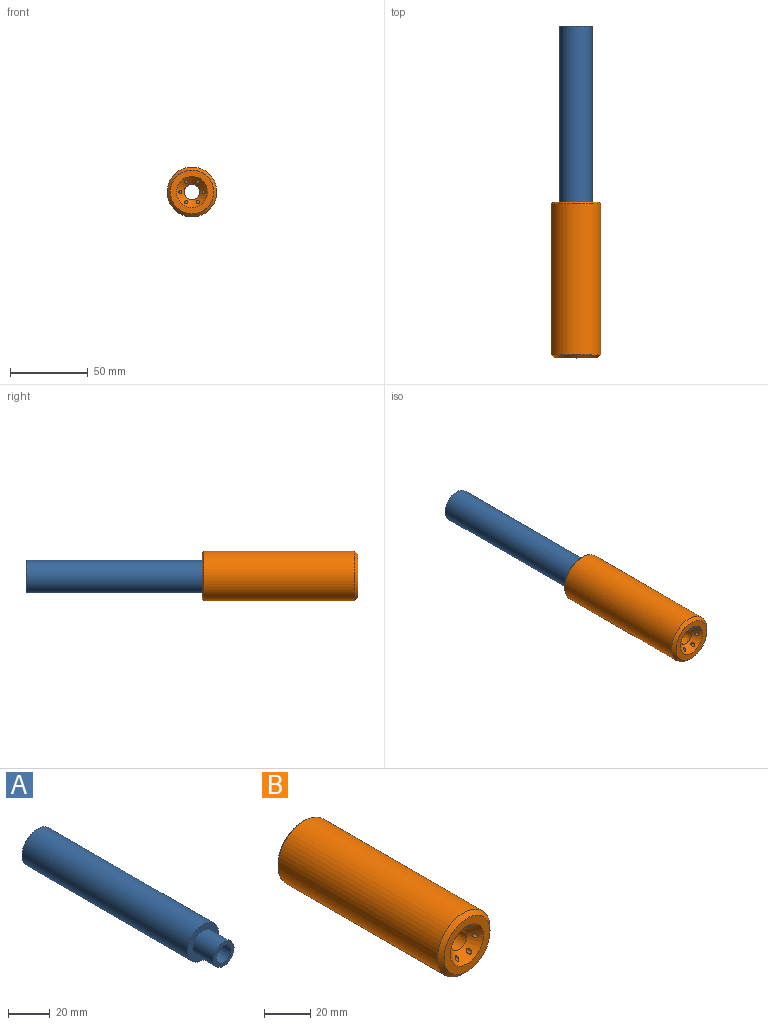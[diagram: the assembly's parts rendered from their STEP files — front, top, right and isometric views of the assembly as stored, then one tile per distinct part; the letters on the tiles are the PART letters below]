
ASSEMBLY  parts=2 mates=1
PART A: 9 faces, bbox 21x127x21 mm
  f0: cylinder r=10.5mm len=113mm, axis (0,1,0), area 7455mm2, adj f1,f2
  f1: plane 21x21mm, normal (0,-1,0), area 192.4mm2, adj f0,f4
  f2: plane 21x21mm, normal (0,1,0), area 91.9mm2, adj f0,f7
  f3: cylinder r=5mm len=111mm, axis (0,1,0), area 3487.2mm2, adj f5,f8
  f4: cylinder r=7mm len=14mm, axis (0,1,0), area 615.8mm2, adj f1,f5
  f5: plane 14x14mm, normal (0,-1,0), area 75.4mm2, adj f3,f4
  f6: cylinder r=7mm len=14mm, axis (0,1,0), area 527.8mm2, adj f7,f8
  f7: cone r=9mm half-angle=45deg, axis (0,1,0), area 142.2mm2, adj f2,f6
  f8: cone r=7mm half-angle=45deg, axis (0,1,0), area 106.6mm2, adj f3,f6
PART B: 173 faces, bbox 32x100x32 mm
  f0: plane 30x30mm, normal (0,1,0), area 493.7mm2, adj f20,f21,f22,f23,f24,f25,f26,f27
  f1: cone r=5mm half-angle=45deg, axis (0,-1,0), area 306.7mm2, adj f3,f4,f8,f10,f12,f14,f16,f18
  f2: cylinder r=16mm len=97mm, axis (0,1,0), area 9751.5mm2, adj f6,f171
  f3: cylinder r=5mm len=79mm, axis (0,1,0), area 2481.9mm2, adj f1,f7
  f4: plane 28x28mm, normal (0,-1,0), area 301.6mm2, adj f1,f6
  f5: cylinder r=7mm len=14mm, axis (0,1,0), area 571.8mm2, adj f7,f172
  f6: cone r=14mm half-angle=45deg, axis (0,1,0), area 266.6mm2, adj f2,f4
  f7: cone r=7mm half-angle=45deg, axis (0,1,0), area 106.6mm2, adj f3,f5
  f8: cylinder r=1mm len=18.5mm, axis (0,1,0), area 110.2mm2, adj f1,f9
  f9: plane 2x2mm, normal (0,-1,0), area 3.1mm2, adj f8
  f10: cylinder r=1mm len=18.5mm, axis (0,1,0), area 110.2mm2, adj f1,f11
  f11: plane 2x2mm, normal (0,-1,0), area 3.1mm2, adj f10
  f12: cylinder r=1mm len=18.5mm, axis (0,1,0), area 110.2mm2, adj f1,f13
  f13: plane 2x2mm, normal (0,-1,0), area 3.1mm2, adj f12
  f14: cylinder r=1mm len=18.5mm, axis (0,1,0), area 110.2mm2, adj f1,f15
  f15: plane 2x2mm, normal (0,-1,0), area 3.1mm2, adj f14
  f16: cylinder r=1mm len=18.5mm, axis (0,1,0), area 110.2mm2, adj f1,f17
  f17: plane 2x2mm, normal (0,-1,0), area 3.1mm2, adj f16
  f18: cylinder r=1mm len=18.5mm, axis (0,1,0), area 110.2mm2, adj f1,f19
  f19: plane 2x2mm, normal (0,-1,0), area 3.1mm2, adj f18
  f20: extruded ~1x0.15mm, area 0.2mm2, adj f0,f21,f36,f37
  f21: extruded ~1x0.23mm, area 0.3mm2, adj f0,f20,f22,f37
  f22: extruded ~1x0.29mm, area 0.3mm2, adj f0,f21,f23,f37
  f23: extruded ~1x0.21mm, area 0.2mm2, adj f0,f22,f24,f37
  f24: extruded ~1x0.2mm, area 0.2mm2, adj f0,f23,f25,f37
  f25: plane 1x0.3mm, normal (-1,0,0), area 0.3mm2, adj f0,f24,f26,f37
  f26: extruded ~1x0.18mm, area 0.2mm2, adj f0,f25,f27,f37
  f27: extruded ~1x0.13mm, area 0.1mm2, adj f0,f26,f28,f37
  f28: extruded ~1x0.16mm, area 0.2mm2, adj f0,f27,f29,f37
  f29: extruded ~1x0.14mm, area 0.2mm2, adj f0,f28,f30,f37
  f30: extruded ~1x0.21mm, area 0.2mm2, adj f0,f29,f31,f37
  f31: plane 1.41x1mm, normal (-1,0,0), area 1.4mm2, adj f0,f30,f32,f37
  f32: plane 1x0.46mm, normal (0,0,1), area 0.5mm2, adj f0,f31,f33,f37
  f33: plane 1.2x1mm, normal (1,0,0), area 1.2mm2, adj f0,f32,f34,f37
  f34: extruded ~1x0.19mm, area 0.2mm2, adj f0,f33,f35,f37
  f35: extruded ~1x0.17mm, area 0.2mm2, adj f0,f34,f36,f37
  f36: extruded ~1x0.16mm, area 0.2mm2, adj f0,f20,f35,f37
  f37: plane 2.16x1.03mm, normal (0,1,0), area 1.1mm2, adj f20,f21,f22,f23,f24,f25,f26,f27
  f38: extruded ~1x0.24mm, area 0.2mm2, adj f0,f39,f53,f54
  f39: extruded ~1x0.2mm, area 0.2mm2, adj f0,f38,f40,f54
  f40: extruded ~1x0.21mm, area 0.2mm2, adj f0,f39,f41,f54
  f41: plane 1x0.3mm, normal (-1,0,0), area 0.3mm2, adj f0,f40,f42,f54
  f42: extruded ~1x0.2mm, area 0.2mm2, adj f0,f41,f43,f54
  f43: extruded ~1x0.11mm, area 0.1mm2, adj f0,f42,f44,f54
  f44: extruded ~1x0.16mm, area 0.2mm2, adj f0,f43,f45,f54
  f45: extruded ~1x0.14mm, area 0.2mm2, adj f0,f44,f46,f54
  f46: extruded ~1x0.21mm, area 0.2mm2, adj f0,f45,f47,f54
  f47: extruded ~1x0.24mm, area 0.2mm2, adj f0,f46,f48,f54
  f48: plane 1.17x1mm, normal (-1,0,0), area 1.2mm2, adj f0,f47,f49,f54
  f49: plane 1x0.46mm, normal (0,0,1), area 0.5mm2, adj f0,f48,f50,f54
  f50: plane 1.46x1mm, normal (1,0,0), area 1.5mm2, adj f0,f49,f51,f54
  f51: extruded ~1x0.28mm, area 0.3mm2, adj f0,f50,f52,f54
  f52: extruded ~1x0.23mm, area 0.3mm2, adj f0,f51,f53,f54
  f53: extruded ~1x0.2mm, area 0.2mm2, adj f0,f38,f52,f54
  f54: plane 2.16x1.03mm, normal (0,1,0), area 1.1mm2, adj f38,f39,f40,f41,f42,f43,f44,f45
  f55: extruded ~1x0.15mm, area 0.2mm2, adj f0,f56,f72,f73
  f56: extruded ~1x0.24mm, area 0.3mm2, adj f0,f55,f57,f73
  f57: extruded ~1x0.29mm, area 0.3mm2, adj f0,f56,f58,f73
  f58: extruded ~1x0.23mm, area 0.2mm2, adj f0,f57,f59,f73
  f59: extruded ~1x0.22mm, area 0.2mm2, adj f0,f58,f60,f73
  f60: plane 1x0.29mm, normal (-1,0,0), area 0.3mm2, adj f0,f59,f61,f73
  f61: extruded ~1x0.17mm, area 0.2mm2, adj f0,f60,f62,f73
  f62: extruded ~1x0.14mm, area 0.1mm2, adj f0,f61,f63,f73
  f63: extruded ~1x0.2mm, area 0.2mm2, adj f0,f62,f64,f73
  f64: extruded ~1x0.14mm, area 0.2mm2, adj f0,f63,f65,f73
  f65: extruded ~1x0.21mm, area 0.2mm2, adj f0,f64,f66,f73
  f66: extruded ~1x0.25mm, area 0.2mm2, adj f0,f65,f67,f73
  f67: plane 1.17x1mm, normal (-1,0,0), area 1.2mm2, adj f0,f66,f68,f73
  f68: plane 1x0.46mm, normal (0,0,1), area 0.5mm2, adj f0,f67,f69,f73
  f69: plane 1.2x1mm, normal (1,0,0), area 1.2mm2, adj f0,f68,f70,f73
  f70: extruded ~1x0.19mm, area 0.2mm2, adj f0,f69,f71,f73
  f71: extruded ~1x0.19mm, area 0.2mm2, adj f0,f70,f72,f73
  f72: extruded ~1x0.18mm, area 0.2mm2, adj f0,f55,f71,f73
  f73: plane 2.16x1.16mm, normal (0,1,0), area 1.1mm2, adj f55,f56,f57,f58,f59,f60,f61,f62
  f74: extruded ~1x0.38mm, area 0.4mm2, adj f0,f75,f89,f90
  f75: plane 1x0.36mm, normal (-1,0,0), area 0.4mm2, adj f0,f74,f76,f90
  f76: extruded ~1x0.18mm, area 0.2mm2, adj f0,f75,f77,f90
  f77: extruded ~1x0.16mm, area 0.2mm2, adj f0,f76,f78,f90
  f78: extruded ~1x0.22mm, area 0.2mm2, adj f0,f77,f79,f90
  f79: extruded ~1x0.26mm, area 0.3mm2, adj f0,f78,f80,f90
  f80: extruded ~1x0.47mm, area 0.5mm2, adj f0,f79,f81,f90
  f81: extruded ~1x0.31mm, area 0.4mm2, adj f0,f80,f82,f90
  f82: plane 1x0.36mm, normal (-1,0,0), area 0.4mm2, adj f0,f81,f83,f90
  f83: extruded ~1x0.37mm, area 0.4mm2, adj f0,f82,f84,f90
  f84: extruded ~1x0.29mm, area 0.4mm2, adj f0,f83,f85,f90
  f85: extruded ~1x0.33mm, area 0.4mm2, adj f0,f84,f86,f90
  f86: extruded ~1x0.41mm, area 0.4mm2, adj f0,f85,f87,f90
  f87: extruded ~1x0.41mm, area 0.4mm2, adj f0,f86,f88,f90
  f88: extruded ~1x0.34mm, area 0.4mm2, adj f0,f87,f89,f90
  f89: extruded ~1x0.29mm, area 0.4mm2, adj f0,f74,f88,f90
  f90: plane 2.17x0.91mm, normal (0,1,0), area 1.1mm2, adj f74,f75,f76,f77,f78,f79,f80,f81
  f91: extruded ~1x0.41mm, area 0.4mm2, adj f0,f92,f106,f107
  f92: extruded ~1x0.41mm, area 0.4mm2, adj f0,f91,f93,f107
  f93: extruded ~1x0.34mm, area 0.4mm2, adj f0,f92,f94,f107
  f94: extruded ~1x0.28mm, area 0.4mm2, adj f0,f93,f95,f107
  f95: extruded ~1x0.38mm, area 0.4mm2, adj f0,f94,f96,f107
  f96: plane 1x0.36mm, normal (1,0,0), area 0.4mm2, adj f0,f95,f97,f107
  f97: extruded ~1x0.18mm, area 0.2mm2, adj f0,f96,f98,f107
  f98: extruded ~1x0.16mm, area 0.2mm2, adj f0,f97,f99,f107
  f99: extruded ~1x0.22mm, area 0.2mm2, adj f0,f98,f100,f107
  f100: extruded ~1x0.27mm, area 0.3mm2, adj f0,f99,f101,f107
  f101: extruded ~1x0.48mm, area 0.5mm2, adj f0,f100,f102,f107
  f102: extruded ~1x0.3mm, area 0.4mm2, adj f0,f101,f103,f107
  f103: plane 1x0.35mm, normal (1,0,0), area 0.4mm2, adj f0,f102,f104,f107
  f104: extruded ~1x0.37mm, area 0.4mm2, adj f0,f103,f105,f107
  f105: extruded ~1x0.29mm, area 0.4mm2, adj f0,f104,f106,f107
  f106: extruded ~1x0.33mm, area 0.4mm2, adj f0,f91,f105,f107
  f107: plane 2.16x0.9mm, normal (0,1,0), area 1.1mm2, adj f91,f92,f93,f94,f95,f96,f97,f98
  f108: plane 1x0.22mm, normal (0.98,0,-0.22), area 0.2mm2, adj f0,f109,f112,f113
  f109: plane 1x0.41mm, normal (0,0,-1), area 0.4mm2, adj f0,f108,f110,f113
  f110: plane 2.14x1mm, normal (-1,0,0), area 2.1mm2, adj f0,f109,f111,f113
  f111: plane 1x0.46mm, normal (0,0,1), area 0.5mm2, adj f0,f110,f112,f113
  f112: plane 1.92x1mm, normal (1,0,0), area 1.9mm2, adj f0,f108,f111,f113
  f113: plane 2.14x0.46mm, normal (0,1,0), area 1mm2, adj f108,f109,f110,f111,f112
  f114: plane 1x0.52mm, normal (0,0,-1), area 0.5mm2, adj f0,f115,f118,f119
  f115: plane 2.07x1mm, normal (-0.96,0,-0.27), area 2.2mm2, adj f0,f114,f116,f119
  f116: plane 1x0.74mm, normal (-1,0,0), area 0.7mm2, adj f0,f115,f117,f119
  f117: plane 1x0.2mm, normal (0,0,1), area 0.2mm2, adj f0,f116,f118,f119
  f118: plane 2.81x1mm, normal (0.95,0,0.31), area 3mm2, adj f0,f114,f117,f119
  f119: plane 2.81x1.11mm, normal (0,1,0), area 1.2mm2, adj f114,f115,f116,f117,f118
  f120: extruded ~1x0.37mm, area 0.4mm2, adj f0,f121,f132,f133
  f121: plane 1x0.36mm, normal (-1,0,0), area 0.4mm2, adj f0,f120,f122,f133
  f122: extruded ~1x0.19mm, area 0.2mm2, adj f0,f121,f123,f133
  f123: extruded ~1x0.15mm, area 0.2mm2, adj f0,f122,f124,f133
  f124: extruded ~1x0.17mm, area 0.2mm2, adj f0,f123,f125,f133
  f125: extruded ~1x0.19mm, area 0.2mm2, adj f0,f124,f126,f133
  f126: plane 1x0.88mm, normal (0,0,-1), area 0.9mm2, adj f0,f125,f127,f133
  f127: plane 1x0.33mm, normal (-1,0,0), area 0.3mm2, adj f0,f126,f128,f133
  f128: plane 1.3x1mm, normal (0,0,1), area 1.3mm2, adj f0,f127,f129,f133
  f129: extruded ~1x0.18mm, area 0.2mm2, adj f0,f128,f130,f133
  f130: extruded ~1x0.39mm, area 0.4mm2, adj f0,f129,f131,f133
  f131: extruded ~1x0.33mm, area 0.4mm2, adj f0,f130,f132,f133
  f132: extruded ~1x0.28mm, area 0.4mm2, adj f0,f120,f131,f133
  f133: plane 1.31x1.24mm, normal (0,1,0), area 0.8mm2, adj f120,f121,f122,f123,f124,f125,f126,f127
  f134: extruded ~1x0.1mm, area 0.1mm2, adj f0,f135,f157,f158
  f135: extruded ~1x0.27mm, area 0.3mm2, adj f0,f134,f136,f158
  f136: extruded ~1x0.19mm, area 0.2mm2, adj f0,f135,f137,f158
  f137: extruded ~1x0.22mm, area 0.2mm2, adj f0,f136,f138,f158
  f138: extruded ~1x0.28mm, area 0.3mm2, adj f0,f137,f139,f158
  f139: extruded ~1x0.2mm, area 0.2mm2, adj f0,f138,f140,f158
  f140: extruded ~1x0.23mm, area 0.2mm2, adj f0,f139,f141,f158
  f141: extruded ~1x0.2mm, area 0.2mm2, adj f0,f140,f142,f158
  f142: extruded ~1x0.23mm, area 0.3mm2, adj f0,f141,f143,f158
  f143: plane 1x0.36mm, normal (1,0,0), area 0.4mm2, adj f0,f142,f144,f158
  f144: extruded ~1x0.35mm, area 0.4mm2, adj f0,f143,f145,f158
  f145: extruded ~1x0.28mm, area 0.4mm2, adj f0,f144,f146,f158
  f146: extruded ~1x0.34mm, area 0.4mm2, adj f0,f145,f147,f158
  f147: extruded ~1x0.41mm, area 0.4mm2, adj f0,f146,f148,f158
  f148: extruded ~1x0.43mm, area 0.4mm2, adj f0,f147,f149,f158
  f149: extruded ~1x0.35mm, area 0.4mm2, adj f0,f148,f150,f158
  f150: extruded ~1x0.31mm, area 0.4mm2, adj f0,f149,f151,f158
  f151: extruded ~1x0.39mm, area 0.4mm2, adj f0,f150,f152,f158
  f152: extruded ~1x0.43mm, area 0.4mm2, adj f0,f151,f153,f158
  f153: extruded ~1x0.29mm, area 0.4mm2, adj f0,f152,f154,f158
  f154: plane 1x0.25mm, normal (0.84,0,-0.55), area 0.3mm2, adj f0,f153,f155,f158
  f155: extruded ~1x0.12mm, area 0.2mm2, adj f0,f154,f156,f158
  f156: extruded ~1x0.14mm, area 0.2mm2, adj f0,f155,f157,f158
  f157: extruded ~1x0.13mm, area 0.1mm2, adj f0,f134,f156,f158
  f158: plane 2.18x1.7mm, normal (0,1,0), area 1.3mm2, adj f134,f135,f136,f137,f138,f139,f140,f141
  f159: plane 1x0.22mm, normal (0.98,0,-0.22), area 0.2mm2, adj f0,f160,f163,f164
  f160: plane 1x0.41mm, normal (0,0,-1), area 0.4mm2, adj f0,f159,f161,f164
  f161: plane 2.14x1mm, normal (-1,0,0), area 2.1mm2, adj f0,f160,f162,f164
  f162: plane 1x0.46mm, normal (0,0,1), area 0.5mm2, adj f0,f161,f163,f164
  f163: plane 1.92x1mm, normal (1,0,0), area 1.9mm2, adj f0,f159,f162,f164
  f164: plane 2.14x0.46mm, normal (0,1,0), area 1mm2, adj f159,f160,f161,f162,f163
  f165: plane 1x0.52mm, normal (0,0,-1), area 0.5mm2, adj f0,f166,f169,f170
  f166: plane 2.81x1mm, normal (-0.96,0,0.3), area 2.9mm2, adj f0,f165,f167,f170
  f167: plane 1x0.24mm, normal (0,0,1), area 0.2mm2, adj f0,f166,f168,f170
  f168: plane 1x0.62mm, normal (1,0,0), area 0.6mm2, adj f0,f167,f169,f170
  f169: plane 2.19x1mm, normal (0.97,0,-0.26), area 2.3mm2, adj f0,f165,f168,f170
  f170: plane 2.81x1.11mm, normal (0,1,0), area 1.2mm2, adj f165,f166,f167,f168,f169
  f171: cone r=16mm half-angle=45deg, axis (0,-1,0), area 137.7mm2, adj f0,f2
  f172: cone r=8mm half-angle=45deg, axis (0,1,0), area 66.6mm2, adj f0,f5
PLACE A at identity
PLACE B t=(0,-193,0.26)mm
MATE fastened B.f0 <-> A.f0  axis (0,1,0) through (0,-113,0)mm
